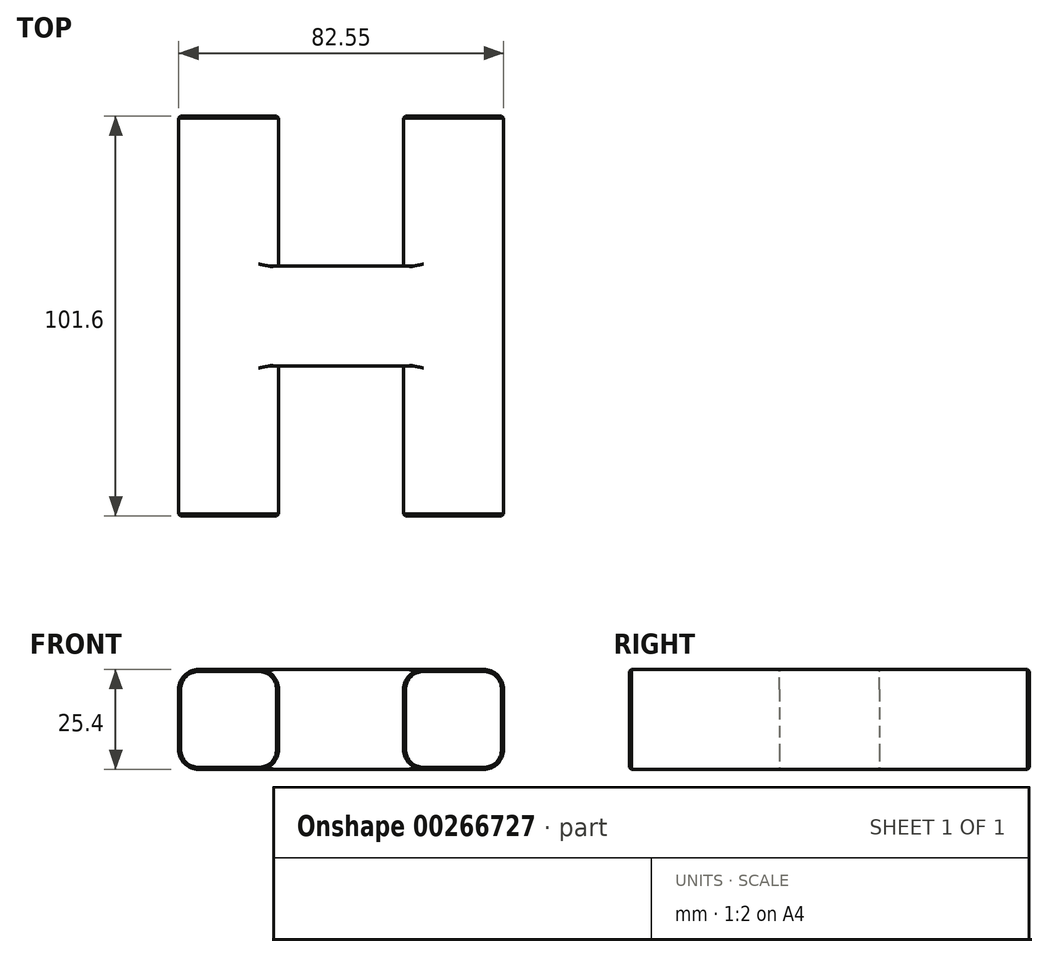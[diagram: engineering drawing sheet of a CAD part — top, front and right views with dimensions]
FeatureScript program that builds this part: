
annotation { "Feature Type Name" : "Feature", "Feature Type Description" : "" }
export const myFeature = defineFeature(function(context is Context, id is Id, definition is map)
    precondition{}
    {
        {
            var Q0;
            Q0=qCreatedBy(makeId("Top.planeOp"),FACE);
            var sketch = newSketch(context, id + "F0", { "sketchPlane" : qUnion([Q0])});
            skLineSegment(sketch, "E0", {"start": v(0, 0) * mm, "end": v(0, -101.6) * mm});
            skLineSegment(sketch, "E1", {"start": v(0, -101.6) * mm, "end": v(25.4, -101.6) * mm});
            skLineSegment(sketch, "E2", {"start": v(25.4, -101.6) * mm, "end": v(25.4, -63.5) * mm});
            skLineSegment(sketch, "E3", {"start": v(25.4, -63.5) * mm, "end": v(57.15, -63.5) * mm});
            skLineSegment(sketch, "E4", {"start": v(57.15, -63.5) * mm, "end": v(57.15, -101.6) * mm});
            skLineSegment(sketch, "E5", {"start": v(57.15, -101.6) * mm, "end": v(82.55, -101.6) * mm});
            skLineSegment(sketch, "E6", {"start": v(82.55, -101.6) * mm, "end": v(82.55, 0) * mm});
            skLineSegment(sketch, "E7", {"start": v(82.55, 0) * mm, "end": v(57.15, 0) * mm});
            skLineSegment(sketch, "E8", {"start": v(57.15, 0) * mm, "end": v(57.15, -38.1) * mm});
            skLineSegment(sketch, "E9", {"start": v(57.15, -38.1) * mm, "end": v(25.4, -38.1) * mm});
            skLineSegment(sketch, "E10", {"start": v(25.4, -38.1) * mm, "end": v(25.4, 0) * mm});
            skLineSegment(sketch, "E11", {"start": v(25.4, 0) * mm, "end": v(0, 0) * mm});
            skSolve(sketch);
        }
        {
            var Q0;
            Q0 = qSketchRegion(id + "F0", true);
            extrude(context, id + "F1", {"entities" : qUnion([Q0]), "depth" : 25.4 * mm});
        }
        {
            var Q0;
            Q0=makeQuery(id+"F1.opExtrude","CAP_EDGE",EDGE,{"disambiguationData":[OSD([sQuery(id+"F0.wireOp",EDGE,"E10")])],"isStart":false});
            var Q1;
            Q1=makeQuery(id+"F1.opExtrude","CAP_EDGE",EDGE,{"disambiguationData":[OSD([sQuery(id+"F0.wireOp",EDGE,"E0")])],"isStart":false});
            var Q2;
            Q2=makeQuery(id+"F1.opExtrude","CAP_EDGE",EDGE,{"disambiguationData":[OSD([sQuery(id+"F0.wireOp",EDGE,"E2")])],"isStart":false});
            var Q3;
            Q3=makeQuery(id+"F1.opExtrude","CAP_EDGE",EDGE,{"disambiguationData":[OSD([sQuery(id+"F0.wireOp",EDGE,"E8")])],"isStart":false});
            var Q4;
            Q4=makeQuery(id+"F1.opExtrude","CAP_EDGE",EDGE,{"disambiguationData":[OSD([sQuery(id+"F0.wireOp",EDGE,"E4")])],"isStart":false});
            var Q5;
            Q5=makeQuery(id+"F1.opExtrude","CAP_EDGE",EDGE,{"disambiguationData":[OSD([sQuery(id+"F0.wireOp",EDGE,"E6")])],"isStart":false});
            var Q6;
            Q6=makeQuery(id+"F1.opExtrude","CAP_EDGE",EDGE,{"disambiguationData":[OSD([sQuery(id+"F0.wireOp",EDGE,"E6")])],"isStart":true});
            var Q7;
            Q7=makeQuery(id+"F1.opExtrude","CAP_EDGE",EDGE,{"disambiguationData":[OSD([sQuery(id+"F0.wireOp",EDGE,"E4")])],"isStart":true});
            var Q8;
            Q8=makeQuery(id+"F1.opExtrude","CAP_EDGE",EDGE,{"disambiguationData":[OSD([sQuery(id+"F0.wireOp",EDGE,"E8")])],"isStart":true});
            var Q9;
            Q9=makeQuery(id+"F1.opExtrude","CAP_EDGE",EDGE,{"disambiguationData":[OSD([sQuery(id+"F0.wireOp",EDGE,"E10")])],"isStart":true});
            var Q10;
            Q10=makeQuery(id+"F1.opExtrude","CAP_EDGE",EDGE,{"disambiguationData":[OSD([sQuery(id+"F0.wireOp",EDGE,"E2")])],"isStart":true});
            var Q11;
            Q11=makeQuery(id+"F1.opExtrude","CAP_EDGE",EDGE,{"disambiguationData":[OSD([sQuery(id+"F0.wireOp",EDGE,"E0")])],"isStart":true});
            fillet(context, id + "F2", {"entities" : qUnion([Q0, Q1, Q2, Q3, Q4, Q5, Q6, Q7, Q8, Q9, Q10, Q11]), "radius" : 5.08 * mm, "tangentPropagation" : true, "allowEdgeOverflow" : false});
        }
        {
            var Q0;
            Q0=makeQuery(id+"F1.opExtrude","CAP_EDGE",EDGE,{"disambiguationData":[OSD([sQuery(id+"F0.wireOp",EDGE,"E11")])],"isStart":false});
            var Q1;
            Q1=makeQuery(id+"F1.opExtrude","CAP_EDGE",EDGE,{"disambiguationData":[OSD([sQuery(id+"F0.wireOp",EDGE,"E7")])],"isStart":false});
            var Q2;
            Q2=makeQuery(id+"F1.opExtrude","CAP_EDGE",EDGE,{"disambiguationData":[OSD([sQuery(id+"F0.wireOp",EDGE,"E5")])],"isStart":false});
            var Q3;
            Q3=makeQuery(id+"F1.opExtrude","CAP_EDGE",EDGE,{"disambiguationData":[OSD([sQuery(id+"F0.wireOp",EDGE,"E1")])],"isStart":false});
            chamfer(context, id + "F3", {"entities" : qUnion([Q0, Q1, Q2, Q3]), "width" : 0.5 * mm, "tangentPropagation" : true});
        }
        {
            var Q0;
            Q0=makeQuery(id+"F1.opExtrude","CAP_EDGE",EDGE,{"disambiguationData":[OSD([sQuery(id+"F0.wireOp",EDGE,"E9")])],"isStart":false});
            var Q1;
            Q1=makeQuery(id+"F1.opExtrude","SWEPT_FACE",FACE,{"disambiguationData":[OSD([sQuery(id+"F0.wireOp",EDGE,"E9")])]});
            var Q2;
            Q2=makeQuery(id+"F1.opExtrude","SWEPT_FACE",FACE,{"disambiguationData":[OSD([sQuery(id+"F0.wireOp",EDGE,"E3")])]});
            fillet(context, id + "F4", {"entities" : qUnion([Q0, Q1, Q2]), "radius" : 0.5 * mm, "tangentPropagation" : true, "allowEdgeOverflow" : false});
        }
    });
